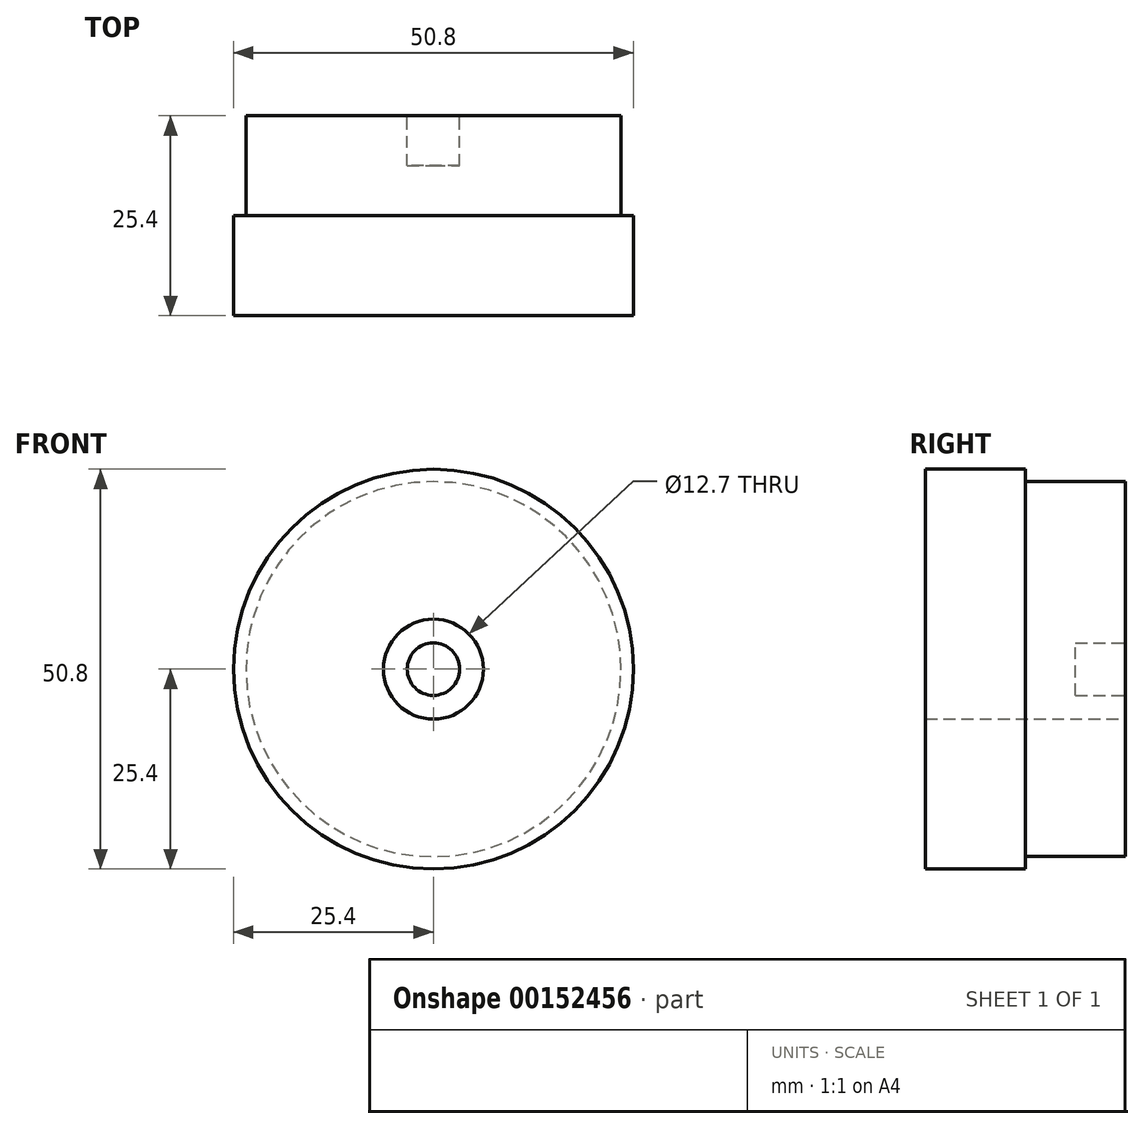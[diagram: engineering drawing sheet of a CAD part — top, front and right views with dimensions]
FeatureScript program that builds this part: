
annotation { "Feature Type Name" : "Feature", "Feature Type Description" : "" }
export const myFeature = defineFeature(function(context is Context, id is Id, definition is map)
    precondition{}
    {
        {
            var Q0;
            Q0=qCreatedBy(makeId("Front.planeOp"),FACE);
            var sketch = newSketch(context, id + "F0", { "sketchPlane" : qUnion([Q0])});
            skCircle(sketch, "E0", {"center": v(0, 0) * mm, "radius": 25.4 * mm});
            skCircle(sketch, "E1", {"center": v(0, 0) * mm, "radius": 6.35 * mm});
            skSolve(sketch);
        }
        {
            var Q0;
            Q0 = qSketchRegion(id + "F0", true);
            extrude(context, id + "F1", {"entities" : qUnion([Q0]), "depth" : 25.4 * mm});
        }
        {
            var Q0;
            Q0=qCreatedBy(makeId("Front.planeOp"),FACE);
            var sketch = newSketch(context, id + "F2", { "sketchPlane" : qUnion([Q0])});
            skCircle(sketch, "E2", {"center": v(0, 0) * mm, "radius": 3.33 * mm});
            skSolve(sketch);
        }
        {
            var Q0;
            Q0 = qSketchRegion(id + "F2", true);
            extrude(context, id + "F3", {"entities" : qUnion([Q0]), "depth" : 6.35 * mm});
        }
        {
            var Q0;
            Q0=qCreatedBy(makeId("Front.planeOp"),FACE);
            var sketch = newSketch(context, id + "F4", { "sketchPlane" : qUnion([Q0])});
            skCircle(sketch, "E3", {"center": v(0, 0) * mm, "radius": 25.4 * mm});
            skCircle(sketch, "E4", {"center": v(0, 0) * mm, "radius": 23.81 * mm});
            skSolve(sketch);
        }
        {
            var Q0;
            Q0 = qSketchRegion(id + "F4", true);
            extrude(context, id + "F5", {"entities" : qUnion([Q0]), "operationType" : NewBodyOperationType.REMOVE, "depth" : 12.7 * mm});
        }
    });
